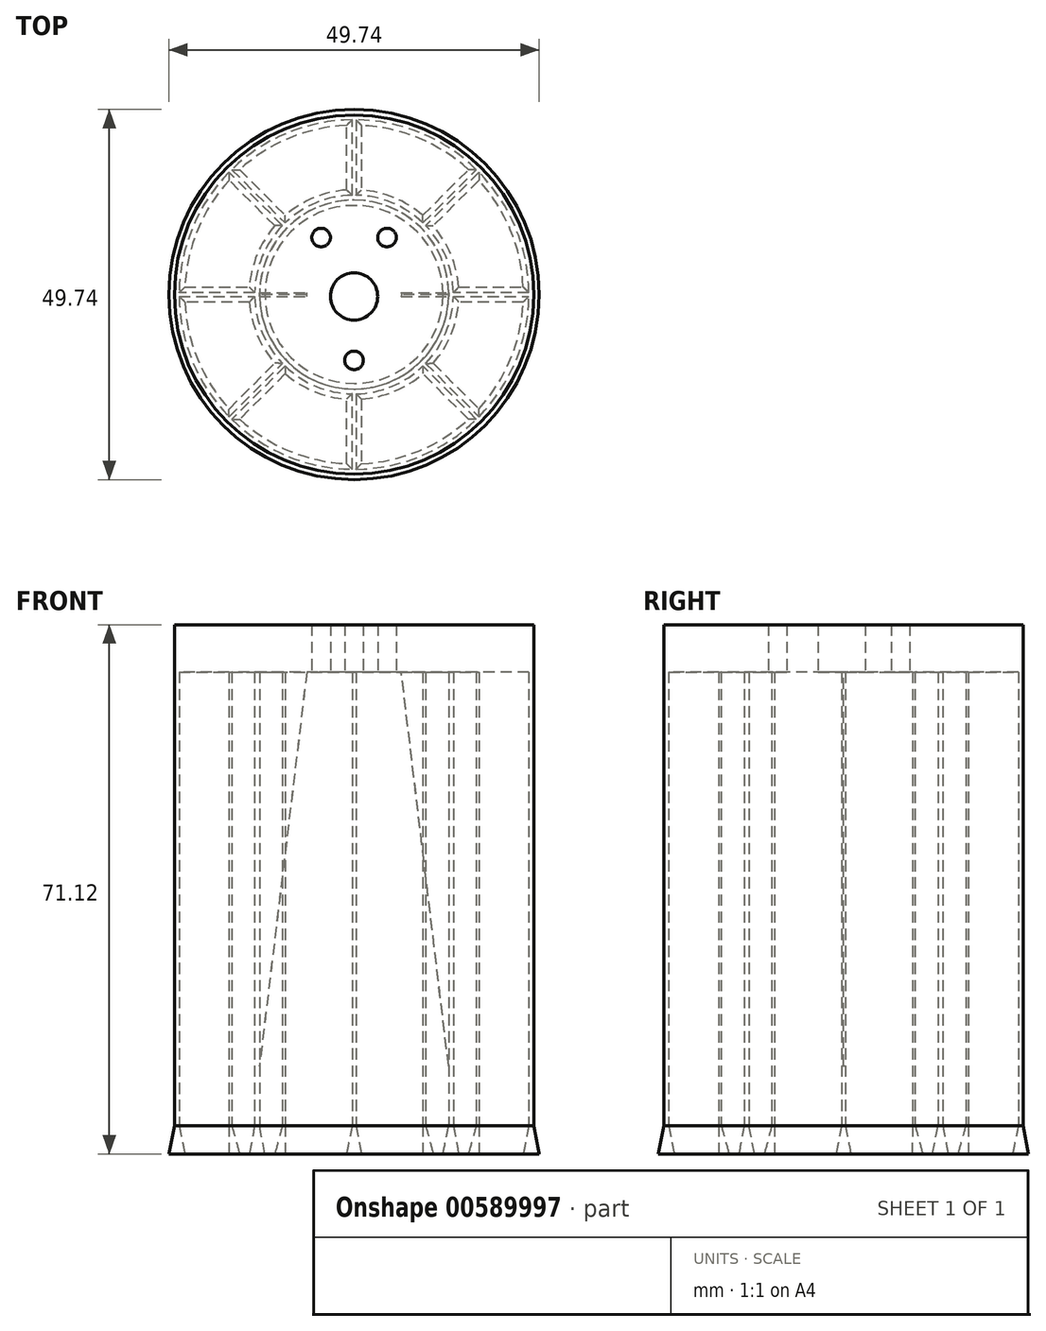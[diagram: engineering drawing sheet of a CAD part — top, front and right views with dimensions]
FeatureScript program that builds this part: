
annotation { "Feature Type Name" : "Feature", "Feature Type Description" : "" }
export const myFeature = defineFeature(function(context is Context, id is Id, definition is map)
    precondition{}
    {
        {
            var Q0;
            Q0=qCreatedBy(makeId("Top.planeOp"),FACE);
            var sketch = newSketch(context, id + "F0", { "sketchPlane" : qUnion([Q0])});
            skCircle(sketch, "E0", {"center": v(0, 0) * mm, "radius": 24.13 * mm});
            skCircle(sketch, "E1", {"center": v(0, 0) * mm, "radius": 23.48 * mm});
            skLineSegment(sketch, "E2", {"start": v(-23.48, 0.25) * mm, "end": v(23.48, 0.25) * mm, "construction": true});
            skLineSegment(sketch, "E3", {"start": v(-23.48, -0.25) * mm, "end": v(23.48, -0.25) * mm, "construction": true});
            skLineSegment(sketch, "E4", {"start": v(0, 0.25) * mm, "end": v(0, -0.25) * mm, "construction": true});
            skCircle(sketch, "E5", {"center": v(0, 0) * mm, "radius": 12.7 * mm});
            skCircle(sketch, "E6", {"center": v(0, 0) * mm, "radius": 13.35 * mm});
            skLineSegment(sketch, "E7", {"start": v(0, 12.7) * mm, "end": v(0, 13.35) * mm, "construction": true});
            skLineSegment(sketch, "E8", {"start": v(0, 23.48) * mm, "end": v(0, 24.13) * mm, "construction": true});
            skLineSegment(sketch, "E9", {"start": v(0, 23.48) * mm, "end": v(0, 23.48) * mm});
            skLineSegment(sketch, "E10", {"start": v(0, 12.7) * mm, "end": v(0.15, 12.7) * mm, "construction": true});
            skLineSegment(sketch, "E11", {"start": v(-13.34, 0.25) * mm, "end": v(-23.48, 0.25) * mm});
            skLineSegment(sketch, "E12", {"start": v(-23.48, -0.25) * mm, "end": v(-13.34, -0.25) * mm});
            skLineSegment(sketch, "E13.1.0", {"start": v(-16.43, -16.78) * mm, "end": v(-9.26, -9.61) * mm});
            skLineSegment(sketch, "E13.1.1", {"start": v(-9.61, -9.26) * mm, "end": v(-16.78, -16.43) * mm});
            skLineSegment(sketch, "E13.2.0", {"start": v(0.25, -23.48) * mm, "end": v(0.25, -13.34) * mm});
            skLineSegment(sketch, "E13.2.1", {"start": v(-0.25, -13.34) * mm, "end": v(-0.25, -23.48) * mm});
            skLineSegment(sketch, "E13.3.0", {"start": v(16.78, -16.43) * mm, "end": v(9.61, -9.26) * mm});
            skLineSegment(sketch, "E13.3.1", {"start": v(9.26, -9.61) * mm, "end": v(16.43, -16.78) * mm});
            skLineSegment(sketch, "E13.4.0", {"start": v(23.48, 0.25) * mm, "end": v(13.34, 0.25) * mm});
            skLineSegment(sketch, "E13.4.1", {"start": v(13.34, -0.25) * mm, "end": v(23.48, -0.25) * mm});
            skLineSegment(sketch, "E13.5.0", {"start": v(16.43, 16.78) * mm, "end": v(9.26, 9.61) * mm});
            skLineSegment(sketch, "E13.5.1", {"start": v(9.61, 9.26) * mm, "end": v(16.78, 16.43) * mm});
            skLineSegment(sketch, "E13.6.0", {"start": v(-0.25, 23.48) * mm, "end": v(-0.25, 13.34) * mm});
            skLineSegment(sketch, "E13.6.1", {"start": v(0.25, 13.34) * mm, "end": v(0.25, 23.48) * mm});
            skLineSegment(sketch, "E13.7.0", {"start": v(-16.78, 16.43) * mm, "end": v(-9.61, 9.26) * mm});
            skLineSegment(sketch, "E13.7.1", {"start": v(-9.26, 9.61) * mm, "end": v(-16.43, 16.78) * mm});
            skCircle(sketch, "E14", {"center": v(4.42, 7.66) * mm, "radius": 1.25 * mm});
            skCircle(sketch, "E15", {"center": v(-4.42, 7.66) * mm, "radius": 1.25 * mm});
            skCircle(sketch, "E16", {"center": v(0, -8.85) * mm, "radius": 1.25 * mm});
            skLineSegment(sketch, "E17", {"start": v(-4.42, 7.66) * mm, "end": v(0, 0) * mm, "construction": true});
            skLineSegment(sketch, "E18", {"start": v(0, 0) * mm, "end": v(4.42, 7.66) * mm, "construction": true});
            skLineSegment(sketch, "E19", {"start": v(0, 0) * mm, "end": v(0, -8.85) * mm, "construction": true});
            skLineSegment(sketch, "E20", {"start": v(-4.42, 7.66) * mm, "end": v(4.42, 7.66) * mm, "construction": true});
            skCircle(sketch, "E21", {"center": v(0, -0.25) * mm, "radius": 3.18 * mm});
            skSolve(sketch);
        }
        {
            var Q0;
            Q0 = qSketchRegion(id + "F0", true);
            var Q1;
            {var subQ0=sQuery(id+"F0.wireOp",EDGE,"E13.5.0");Q1=makeQuery(id+"F0.imprint","IMPRINT",FACE,{"disambiguationData":[TD([[makeQuery(id+"F0.imprint","IMPRINT",EDGE,{"derivedFrom":subQ0}),1.0]])]});}
            var Q2;
            {var subQ0=sQuery(id+"F0.wireOp",EDGE,"E13.6.0");Q2=makeQuery(id+"F0.imprint","IMPRINT",FACE,{"disambiguationData":[TD([[makeQuery(id+"F0.imprint","IMPRINT",EDGE,{"derivedFrom":subQ0}),1.0]])]});}
            var Q3;
            Q3=makeQuery(id+"F0.imprint","IMPRINT",FACE,{"disambiguationData":[TD([[makeQuery(id+"F0.imprint","IMPRINT",EDGE,{"derivedFrom":sQuery(id+"F0.wireOp",EDGE,"E5")}),-1.0]])]});
            var Q4;
            {var subQ0=sQuery(id+"F0.wireOp",EDGE,"E13.7.0");Q4=makeQuery(id+"F0.imprint","IMPRINT",FACE,{"disambiguationData":[TD([[makeQuery(id+"F0.imprint","IMPRINT",EDGE,{"derivedFrom":subQ0}),1.0]])]});}
            var Q5;
            {var subQ0=sQuery(id+"F0.wireOp",EDGE,"E11");Q5=makeQuery(id+"F0.imprint","IMPRINT",FACE,{"disambiguationData":[TD([[makeQuery(id+"F0.imprint","IMPRINT",EDGE,{"derivedFrom":subQ0}),1.0]])]});}
            var Q6;
            {var subQ0=sQuery(id+"F0.wireOp",EDGE,"E13.1.0");Q6=makeQuery(id+"F0.imprint","IMPRINT",FACE,{"disambiguationData":[TD([[makeQuery(id+"F0.imprint","IMPRINT",EDGE,{"derivedFrom":subQ0}),1.0]])]});}
            var Q7;
            {var subQ0=sQuery(id+"F0.wireOp",EDGE,"E13.2.0");Q7=makeQuery(id+"F0.imprint","IMPRINT",FACE,{"disambiguationData":[TD([[makeQuery(id+"F0.imprint","IMPRINT",EDGE,{"derivedFrom":subQ0}),1.0]])]});}
            var Q8;
            {var subQ0=sQuery(id+"F0.wireOp",EDGE,"E13.3.0");Q8=makeQuery(id+"F0.imprint","IMPRINT",FACE,{"disambiguationData":[TD([[makeQuery(id+"F0.imprint","IMPRINT",EDGE,{"derivedFrom":subQ0}),1.0]])]});}
            var Q9;
            {var subQ0=sQuery(id+"F0.wireOp",EDGE,"E13.4.0");Q9=makeQuery(id+"F0.imprint","IMPRINT",FACE,{"disambiguationData":[TD([[makeQuery(id+"F0.imprint","IMPRINT",EDGE,{"derivedFrom":subQ0}),1.0]])]});}
            extrude(context, id + "F1", {"entities" : qUnion([Q0, Q1, Q2, Q3, Q4, Q5, Q6, Q7, Q8, Q9]), "depth" : 60.96 * mm, "offsetDistance" : 25.4 * mm, "hasSecondDirection" : true, "secondDirectionOppositeDirection" : true, "secondDirectionDepth" : 3.8 * mm, "hasSecondDirectionDraft" : true, "secondDirectionDraftAngle" : 11 * degree});
        }
        {
            var Q0;
            Q0=makeQuery(id+"F0.imprint","IMPRINT",FACE,{"disambiguationData":[TD([[makeQuery(id+"F0.imprint","IMPRINT",EDGE,{"derivedFrom":sQuery(id+"F0.wireOp",EDGE,"E0")}),1.0]])]});
            var Q1;
            {var subQ0=sQuery(id+"F0.wireOp",EDGE,"E11");Q1=makeQuery(id+"F0.imprint","IMPRINT",FACE,{"disambiguationData":[TD([[makeQuery(id+"F0.imprint","IMPRINT",EDGE,{"derivedFrom":subQ0}),-1.0]])]});}
            var Q2;
            {var subQ0=sQuery(id+"F0.wireOp",EDGE,"E12");Q2=makeQuery(id+"F0.imprint","IMPRINT",FACE,{"disambiguationData":[TD([[makeQuery(id+"F0.imprint","IMPRINT",EDGE,{"derivedFrom":subQ0}),-1.0]])]});}
            var Q3;
            {var subQ0=sQuery(id+"F0.wireOp",EDGE,"E13.1.0");Q3=makeQuery(id+"F0.imprint","IMPRINT",FACE,{"disambiguationData":[TD([[makeQuery(id+"F0.imprint","IMPRINT",EDGE,{"derivedFrom":subQ0}),-1.0]])]});}
            var Q4;
            {var subQ0=sQuery(id+"F0.wireOp",EDGE,"E13.2.0");Q4=makeQuery(id+"F0.imprint","IMPRINT",FACE,{"disambiguationData":[TD([[makeQuery(id+"F0.imprint","IMPRINT",EDGE,{"derivedFrom":subQ0}),-1.0]])]});}
            var Q5;
            {var subQ0=sQuery(id+"F0.wireOp",EDGE,"E13.3.0");Q5=makeQuery(id+"F0.imprint","IMPRINT",FACE,{"disambiguationData":[TD([[makeQuery(id+"F0.imprint","IMPRINT",EDGE,{"derivedFrom":subQ0}),-1.0]])]});}
            var Q6;
            {var subQ0=sQuery(id+"F0.wireOp",EDGE,"E13.4.0");Q6=makeQuery(id+"F0.imprint","IMPRINT",FACE,{"disambiguationData":[TD([[makeQuery(id+"F0.imprint","IMPRINT",EDGE,{"derivedFrom":subQ0}),-1.0]])]});}
            var Q7;
            {var subQ0=sQuery(id+"F0.wireOp",EDGE,"E13.5.0");Q7=makeQuery(id+"F0.imprint","IMPRINT",FACE,{"disambiguationData":[TD([[makeQuery(id+"F0.imprint","IMPRINT",EDGE,{"derivedFrom":subQ0}),-1.0]])]});}
            var Q8;
            {var subQ0=sQuery(id+"F0.wireOp",EDGE,"E13.6.0");Q8=makeQuery(id+"F0.imprint","IMPRINT",FACE,{"disambiguationData":[TD([[makeQuery(id+"F0.imprint","IMPRINT",EDGE,{"derivedFrom":subQ0}),-1.0]])]});}
            var Q9;
            Q9=makeQuery(id+"F0.imprint","IMPRINT",FACE,{"disambiguationData":[TD([[makeQuery(id+"F0.imprint","IMPRINT",EDGE,{"derivedFrom":sQuery(id+"F0.wireOp",EDGE,"E5")}),1.0]])]});
            var Q10;
            {var subQ0=sQuery(id+"F0.wireOp",EDGE,"E13.7.0");Q10=makeQuery(id+"F0.imprint","IMPRINT",FACE,{"disambiguationData":[TD([[makeQuery(id+"F0.imprint","IMPRINT",EDGE,{"derivedFrom":subQ0}),1.0]])]});}
            var Q11;
            {var subQ0=sQuery(id+"F0.wireOp",EDGE,"E11");Q11=makeQuery(id+"F0.imprint","IMPRINT",FACE,{"disambiguationData":[TD([[makeQuery(id+"F0.imprint","IMPRINT",EDGE,{"derivedFrom":subQ0}),1.0]])]});}
            var Q12;
            {var subQ0=sQuery(id+"F0.wireOp",EDGE,"E13.1.0");Q12=makeQuery(id+"F0.imprint","IMPRINT",FACE,{"disambiguationData":[TD([[makeQuery(id+"F0.imprint","IMPRINT",EDGE,{"derivedFrom":subQ0}),1.0]])]});}
            var Q13;
            {var subQ0=sQuery(id+"F0.wireOp",EDGE,"E13.2.0");Q13=makeQuery(id+"F0.imprint","IMPRINT",FACE,{"disambiguationData":[TD([[makeQuery(id+"F0.imprint","IMPRINT",EDGE,{"derivedFrom":subQ0}),1.0]])]});}
            var Q14;
            {var subQ0=sQuery(id+"F0.wireOp",EDGE,"E13.3.0");Q14=makeQuery(id+"F0.imprint","IMPRINT",FACE,{"disambiguationData":[TD([[makeQuery(id+"F0.imprint","IMPRINT",EDGE,{"derivedFrom":subQ0}),1.0]])]});}
            var Q15;
            {var subQ0=sQuery(id+"F0.wireOp",EDGE,"E13.4.0");Q15=makeQuery(id+"F0.imprint","IMPRINT",FACE,{"disambiguationData":[TD([[makeQuery(id+"F0.imprint","IMPRINT",EDGE,{"derivedFrom":subQ0}),1.0]])]});}
            var Q16;
            {var subQ0=sQuery(id+"F0.wireOp",EDGE,"E13.5.0");Q16=makeQuery(id+"F0.imprint","IMPRINT",FACE,{"disambiguationData":[TD([[makeQuery(id+"F0.imprint","IMPRINT",EDGE,{"derivedFrom":subQ0}),1.0]])]});}
            var Q17;
            {var subQ0=sQuery(id+"F0.wireOp",EDGE,"E13.6.0");Q17=makeQuery(id+"F0.imprint","IMPRINT",FACE,{"disambiguationData":[TD([[makeQuery(id+"F0.imprint","IMPRINT",EDGE,{"derivedFrom":subQ0}),1.0]])]});}
            var Q18;
            Q18=makeQuery(id+"F0.imprint","IMPRINT",FACE,{"disambiguationData":[TD([[makeQuery(id+"F0.imprint","IMPRINT",EDGE,{"derivedFrom":sQuery(id+"F0.wireOp",EDGE,"E5")}),-1.0]])]});
            extrude(context, id + "F2", {"entities" : qUnion([Q0, Q1, Q2, Q3, Q4, Q5, Q6, Q7, Q8, Q9, Q10, Q11, Q12, Q13, Q14, Q15, Q16, Q17, Q18]), "operationType" : NewBodyOperationType.ADD, "depth" : 67.3 * mm, "offsetDistance" : 25.4 * mm, "hasSecondDirection" : true, "secondDirectionOppositeDirection" : false, "secondDirectionDepth" : 60.96 * mm});
        }
        {
            var Q0;
            Q0=qCreatedBy(makeId("Front.planeOp"),FACE);
            var sketch = newSketch(context, id + "F3", { "sketchPlane" : qUnion([Q0])});
            skLineSegment(sketch, "E22", {"start": v(6.35, 60.96) * mm, "end": v(14.05, 60.96) * mm});
            skLineSegment(sketch, "E23", {"start": v(14.05, 60.96) * mm, "end": v(14.05, -3.17) * mm});
            skLineSegment(sketch, "E24", {"start": v(14.05, -3.18) * mm, "end": v(6.35, 60.96) * mm});
            skPoint(sketch, "E25", {"position": v(0, 51.35) * mm});
            skLineSegment(sketch, "E26", {"start": v(0, 51.35) * mm, "end": v(0, 60.96) * mm, "construction": true});
            skLineSegment(sketch, "E27.MirrorCS", {"start": v(-14.05, 60.96) * mm, "end": v(-14.05, -3.17) * mm});
            skLineSegment(sketch, "E28.MirrorCS", {"start": v(-14.05, -3.17) * mm, "end": v(-6.35, 60.96) * mm});
            skLineSegment(sketch, "E29.MirrorCS", {"start": v(-6.35, 60.96) * mm, "end": v(-14.05, 60.96) * mm});
            skPoint(sketch, "E30", {"position": v(14.05, -3.81) * mm});
            skSolve(sketch);
        }
        {
            var Q0;
            Q0 = qSketchRegion(id + "F3", true);
            extrude(context, id + "F4", {"entities" : qUnion([Q0]), "operationType" : NewBodyOperationType.ADD, "depth" : 0.25 * mm, "offsetDistance" : 25.4 * mm, "hasDraft" : true, "draftAngle" : 3 * degree, "hasSecondDirection" : true, "secondDirectionOppositeDirection" : true, "secondDirectionDepth" : 0.25 * mm, "hasSecondDirectionDraft" : true, "secondDirectionDraftAngle" : 3 * degree});
        }
    });
